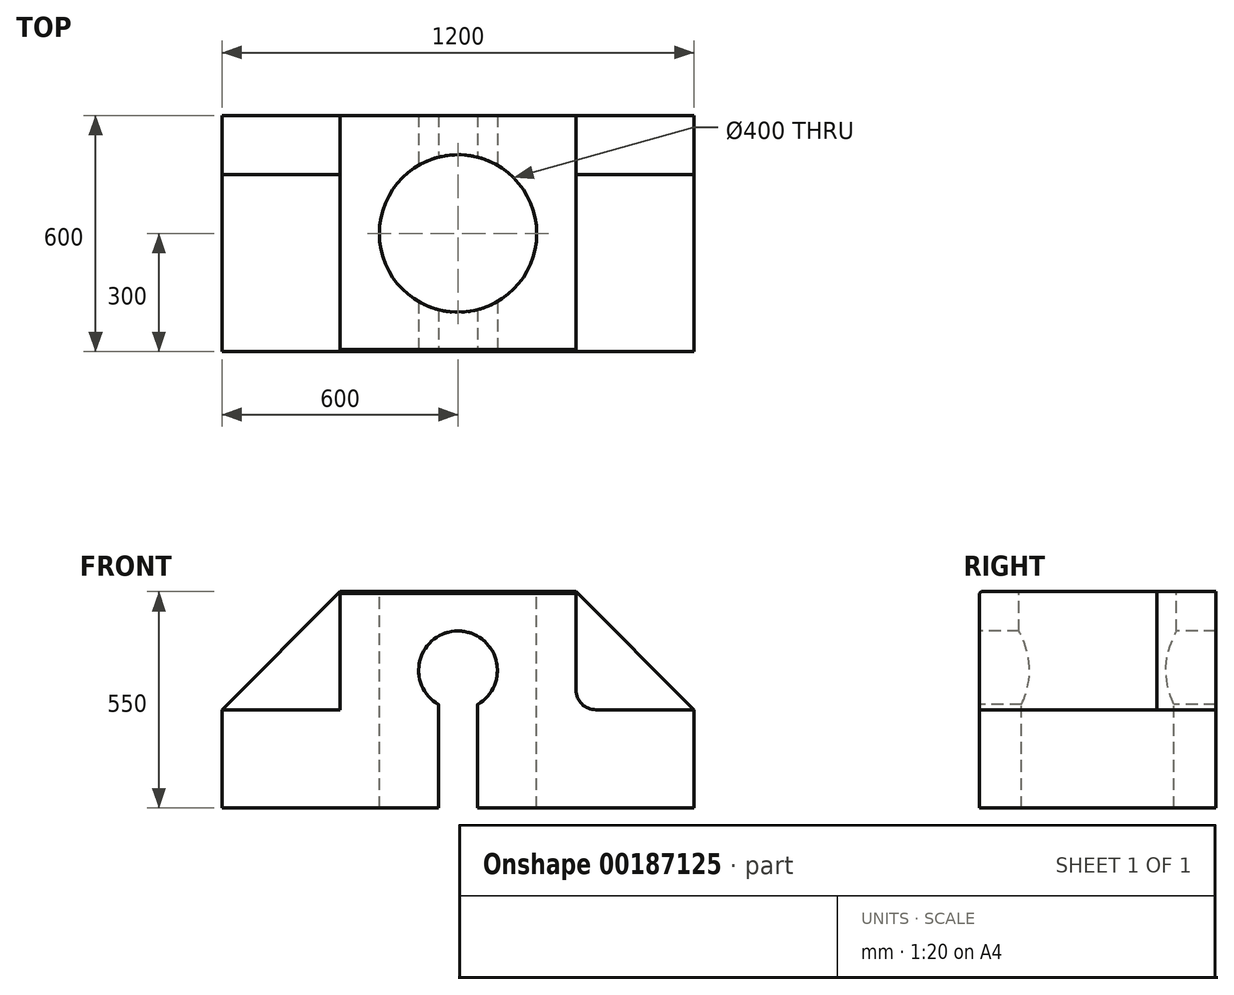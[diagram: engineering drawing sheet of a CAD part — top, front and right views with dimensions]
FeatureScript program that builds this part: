
annotation { "Feature Type Name" : "Feature", "Feature Type Description" : "" }
export const myFeature = defineFeature(function(context is Context, id is Id, definition is map)
    precondition{}
    {
        {
            var Q0;
            Q0=qCreatedBy(makeId("Top.planeOp"),FACE);
            var sketch = newSketch(context, id + "F0", { "sketchPlane" : qUnion([Q0])});
            skLineSegment(sketch, "E0.bottom", {"start": v(600, 300) * mm, "end": v(-600, 300) * mm});
            skLineSegment(sketch, "E0.top", {"start": v(600, -300) * mm, "end": v(-600, -300) * mm});
            skLineSegment(sketch, "E0.left", {"start": v(600, 300) * mm, "end": v(600, -300) * mm});
            skLineSegment(sketch, "E0.right", {"start": v(-600, 300) * mm, "end": v(-600, -300) * mm});
            skPoint(sketch, "E0.middle", {"position": v(0, 0) * mm});
            skSolve(sketch);
        }
        {
            var Q0;
            Q0 = qSketchRegion(id + "F0", true);
            extrude(context, id + "F1", {"entities" : qUnion([Q0]), "depth" : 250 * mm});
        }
        {
            var Q0;
            Q0=makeQuery(id+"F1.opExtrude","CAP_FACE",FACE,{"disambiguationData":[OSD([sQuery(id+"F0.wireOp",EDGE,"E0.bottom"),sQuery(id+"F0.wireOp",EDGE,"E0.top"),sQuery(id+"F0.wireOp",EDGE,"E0.left"),sQuery(id+"F0.wireOp",EDGE,"E0.right")])],"isStart":false});
            var sketch = newSketch(context, id + "F2", { "sketchPlane" : qUnion([Q0])});
            skLineSegment(sketch, "E1.bottom", {"start": v(300, 300) * mm, "end": v(-300, 300) * mm});
            skLineSegment(sketch, "E1.top", {"start": v(300, -300) * mm, "end": v(-300, -300) * mm});
            skLineSegment(sketch, "E1.left", {"start": v(300, 300) * mm, "end": v(300, -300) * mm});
            skLineSegment(sketch, "E1.right", {"start": v(-300, 300) * mm, "end": v(-300, -300) * mm});
            skPoint(sketch, "E1.middle", {"position": v(0, 0) * mm});
            skSolve(sketch);
        }
        {
            var Q0;
            Q0 = qSketchRegion(id + "F2", true);
            extrude(context, id + "F3", {"entities" : qUnion([Q0]), "operationType" : NewBodyOperationType.ADD, "depth" : 300 * mm});
        }
        {
            var Q0;
            Q0=makeQuery(id+"F3.opExtrude","CAP_FACE",FACE,{"disambiguationData":[OSD([sQuery(id+"F2.wireOp",EDGE,"E1.bottom"),sQuery(id+"F2.wireOp",EDGE,"E1.top"),sQuery(id+"F2.wireOp",EDGE,"E1.left"),sQuery(id+"F2.wireOp",EDGE,"E1.right")])],"isStart":false});
            var sketch = newSketch(context, id + "F4", { "sketchPlane" : qUnion([Q0])});
            skCircle(sketch, "E2", {"center": v(0, 0) * mm, "radius": 200 * mm});
            skSolve(sketch);
        }
        {
            var Q0;
            Q0 = qSketchRegion(id + "F4", true);
            extrude(context, id + "F5", {"entities" : qUnion([Q0]), "operationType" : NewBodyOperationType.REMOVE, "endBound" : BoundingType.THROUGH_ALL, "oppositeDirection" : true, "depth" : 25 * mm});
        }
        {
            var Q0;
            {var subQ0=sQuery(id+"F0.wireOp",EDGE,"E0.left");var subQ1=sQuery(id+"F0.wireOp",EDGE,"E0.top");var subQ2=sQuery(id+"F0.wireOp",EDGE,"E0.bottom");Q0=makeQuery(id+"F3.boolean.opBoolean","SPLIT",FACE,{"disambiguationData":[TD([makeQuery(id+"F1.opExtrude","SWEPT_FACE",FACE,{"disambiguationData":[OSD([subQ0])]})])],"derivedFrom":makeQuery(id+"F1.opExtrude","CAP_FACE",FACE,{"disambiguationData":[OSD([subQ2,subQ1,subQ0,sQuery(id+"F0.wireOp",EDGE,"E0.right")])],"isStart":false})});}
            var sketch = newSketch(context, id + "F6", { "sketchPlane" : qUnion([Q0])});
            skLineSegment(sketch, "E3.bottom", {"start": v(300, 300) * mm, "end": v(600, 300) * mm});
            skLineSegment(sketch, "E3.top", {"start": v(300, 150) * mm, "end": v(600, 150) * mm});
            skLineSegment(sketch, "E3.left", {"start": v(300, 300) * mm, "end": v(300, 150) * mm});
            skLineSegment(sketch, "E3.right", {"start": v(600, 300) * mm, "end": v(600, 150) * mm});
            skSolve(sketch);
        }
        {
            var Q0;
            Q0 = qSketchRegion(id + "F6", true);
            extrude(context, id + "F7", {"entities" : qUnion([Q0]), "operationType" : NewBodyOperationType.ADD, "depth" : 300 * mm});
        }
        {
            var Q0;
            {var subQ0=sQuery(id+"F0.wireOp",EDGE,"E0.right");var subQ1=sQuery(id+"F0.wireOp",EDGE,"E0.top");var subQ2=sQuery(id+"F0.wireOp",EDGE,"E0.bottom");Q0=makeQuery(id+"F3.boolean.opBoolean","SPLIT",FACE,{"disambiguationData":[TD([makeQuery(id+"F1.opExtrude","SWEPT_FACE",FACE,{"disambiguationData":[OSD([subQ0])]})])],"derivedFrom":makeQuery(id+"F1.opExtrude","CAP_FACE",FACE,{"disambiguationData":[OSD([subQ2,subQ1,sQuery(id+"F0.wireOp",EDGE,"E0.left"),subQ0])],"isStart":false})});}
            var sketch = newSketch(context, id + "F8", { "sketchPlane" : qUnion([Q0])});
            skLineSegment(sketch, "E4.bottom", {"start": v(-300, 300) * mm, "end": v(-600, 300) * mm});
            skLineSegment(sketch, "E4.top", {"start": v(-300, 150) * mm, "end": v(-600, 150) * mm});
            skLineSegment(sketch, "E4.left", {"start": v(-300, 300) * mm, "end": v(-300, 150) * mm});
            skLineSegment(sketch, "E4.right", {"start": v(-600, 300) * mm, "end": v(-600, 150) * mm});
            skSolve(sketch);
        }
        {
            var Q0;
            Q0=makeQuery(id+"F8.imprint","IMPRINT",FACE,{"disambiguationData":[TD([[makeQuery(id+"F8.imprint","IMPRINT",EDGE,{"derivedFrom":sQuery(id+"F8.wireOp",EDGE,"E4.bottom")}),1.0]])]});
            extrude(context, id + "F9", {"entities" : qUnion([Q0]), "operationType" : NewBodyOperationType.ADD, "depth" : 300 * mm});
        }
        {
            var Q0;
            Q0=makeQuery(id+"F3.boolean.opBoolean","MERGE",FACE,{"derivedFrom":[makeQuery(id+"F1.opExtrude","SWEPT_FACE",FACE,{"disambiguationData":[OSD([sQuery(id+"F0.wireOp",EDGE,"E0.top")])]}),makeQuery(id+"F3.opExtrude","SWEPT_FACE",FACE,{"disambiguationData":[OSD([sQuery(id+"F2.wireOp",EDGE,"E1.top")])]})]});
            var sketch = newSketch(context, id + "F10", { "sketchPlane" : qUnion([Q0])});
            skCircle(sketch, "E5", {"center": v(0, 350) * mm, "radius": 100 * mm});
            skLineSegment(sketch, "E6.bottom", {"start": v(-50, 0) * mm, "end": v(50, 0) * mm});
            skLineSegment(sketch, "E7", {"start": v(-50, 0) * mm, "end": v(-50, 263.4) * mm});
            skLineSegment(sketch, "E8", {"start": v(50, 0) * mm, "end": v(50, 263.4) * mm});
            skSolve(sketch);
        }
        {
            var Q0;
            Q0 = qSketchRegion(id + "F10", true);
            extrude(context, id + "F11", {"entities" : qUnion([Q0]), "operationType" : NewBodyOperationType.REMOVE, "endBound" : BoundingType.THROUGH_ALL, "oppositeDirection" : true, "depth" : 25 * mm});
        }
        {
            var Q0;
            Q0=makeQuery(id+"F7.opExtrude","SWEPT_FACE",FACE,{"disambiguationData":[OSD([sQuery(id+"F6.wireOp",EDGE,"E3.top")])]});
            var sketch = newSketch(context, id + "F12", { "sketchPlane" : qUnion([Q0])});
            skLineSegment(sketch, "E9", {"start": v(300, 550) * mm, "end": v(600, 250) * mm});
            skLineSegment(sketch, "E10", {"start": v(600, 250) * mm, "end": v(600, 550) * mm});
            skLineSegment(sketch, "E11", {"start": v(600, 550) * mm, "end": v(300, 550) * mm});
            skSolve(sketch);
        }
        {
            var Q0;
            Q0 = qSketchRegion(id + "F12", true);
            extrude(context, id + "F13", {"entities" : qUnion([Q0]), "operationType" : NewBodyOperationType.REMOVE, "endBound" : BoundingType.THROUGH_ALL, "oppositeDirection" : true, "depth" : 25 * mm});
        }
        {
            var Q0;
            Q0=makeQuery(id+"F9.opExtrude","SWEPT_FACE",FACE,{"disambiguationData":[OSD([sQuery(id+"F8.wireOp",EDGE,"E4.top")])]});
            var sketch = newSketch(context, id + "F14", { "sketchPlane" : qUnion([Q0])});
            skLineSegment(sketch, "E12", {"start": v(-300, 550) * mm, "end": v(-600, 250) * mm});
            skLineSegment(sketch, "E13", {"start": v(-600, 250) * mm, "end": v(-600, 550) * mm});
            skLineSegment(sketch, "E14", {"start": v(-600, 550) * mm, "end": v(-300, 550) * mm});
            skSolve(sketch);
        }
        {
            var Q0;
            Q0=makeQuery(id+"F14.imprint","IMPRINT",FACE,{"disambiguationData":[TD([[makeQuery(id+"F14.imprint","IMPRINT",EDGE,{"derivedFrom":sQuery(id+"F14.wireOp",EDGE,"E12")}),-1.0]])]});
            extrude(context, id + "F15", {"entities" : qUnion([Q0]), "operationType" : NewBodyOperationType.REMOVE, "endBound" : BoundingType.THROUGH_ALL, "oppositeDirection" : true, "depth" : 25 * mm});
        }
        {
            var Q0;
            Q0=makeQuery(id+"F3.opExtrude","CAP_EDGE",EDGE,{"disambiguationData":[OSD([sQuery(id+"F2.wireOp",EDGE,"E1.left")])],"isStart":true});
            fillet(context, id + "F16", {"entities" : qUnion([Q0]), "radius" : 50 * mm, "tangentPropagation" : true, "allowEdgeOverflow" : false});
        }
        {
            var Q0;
            Q0=makeQuery(id+"F3.opExtrude","CAP_EDGE",EDGE,{"disambiguationData":[OSD([sQuery(id+"F2.wireOp",EDGE,"E1.top")])],"isStart":false});
            chamfer(context, id + "F17", {"entities" : qUnion([Q0]), "chamferType" : ChamferType.OFFSET_ANGLE, "width" : 5 * mm, "oppositeDirection" : false, "angle" : 45 * degree, "tangentPropagation" : true});
        }
    });
